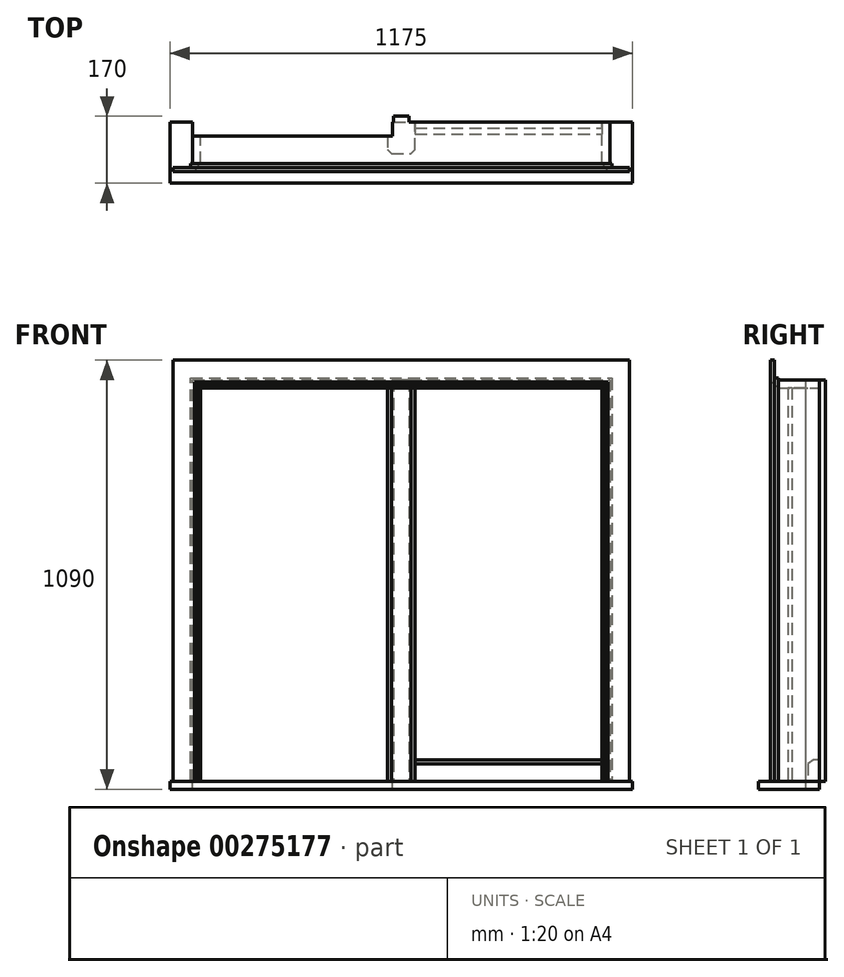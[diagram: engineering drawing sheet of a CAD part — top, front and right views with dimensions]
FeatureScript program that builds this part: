
annotation { "Feature Type Name" : "Feature", "Feature Type Description" : "" }
export const myFeature = defineFeature(function(context is Context, id is Id, definition is map)
    precondition{}
    {
        {
            var Q0;
            Q0=qCreatedBy(makeId("Top.planeOp"),FACE);
            var sketch = newSketch(context, id + "F0", { "sketchPlane" : qUnion([Q0])});
            skLineSegment(sketch, "E0.bottom", {"start": v(-530, -105) * mm, "end": v(-510, -105) * mm});
            skLineSegment(sketch, "E0.top", {"start": v(-530, 0) * mm, "end": v(-510, 0) * mm});
            skLineSegment(sketch, "E0.left", {"start": v(-530, -105) * mm, "end": v(-530, 0) * mm});
            skLineSegment(sketch, "E0.right", {"start": v(-510, -105) * mm, "end": v(-510, 0) * mm});
            skLineSegment(sketch, "E1.bottom", {"start": v(510, -105) * mm, "end": v(530, -105) * mm});
            skLineSegment(sketch, "E1.top", {"start": v(510, 0) * mm, "end": v(530, 0) * mm});
            skLineSegment(sketch, "E1.left", {"start": v(510, -105) * mm, "end": v(510, 0) * mm});
            skLineSegment(sketch, "E1.right", {"start": v(530, -105) * mm, "end": v(530, 0) * mm});
            skLineSegment(sketch, "E2", {"start": v(0, 0) * mm, "end": v(-35, 0) * mm});
            skLineSegment(sketch, "E3", {"start": v(-35, 0) * mm, "end": v(-35, -70) * mm});
            skLineSegment(sketch, "E4", {"start": v(-35, -70) * mm, "end": v(-25, -80) * mm});
            skLineSegment(sketch, "E5", {"start": v(-25, -80) * mm, "end": v(25, -80) * mm});
            skLineSegment(sketch, "E6", {"start": v(25, -80) * mm, "end": v(35, -70) * mm});
            skLineSegment(sketch, "E7", {"start": v(35, -70) * mm, "end": v(35, 0) * mm});
            skLineSegment(sketch, "E8", {"start": v(35, 0) * mm, "end": v(0, 0) * mm});
            skSolve(sketch);
        }
        {
            var Q0;
            Q0 = qSketchRegion(id + "F0", true);
            extrude(context, id + "F1", {"entities" : qUnion([Q0]), "depth" : 1000 * mm, "offsetDistance" : 25 * mm});
        }
        {
            var Q0;
            Q0=makeQuery(id+"F1.opExtrude","CAP_FACE",FACE,{"disambiguationData":[OSD([sQuery(id+"F0.wireOp",EDGE,"E0.bottom"),sQuery(id+"F0.wireOp",EDGE,"E0.top"),sQuery(id+"F0.wireOp",EDGE,"E0.left"),sQuery(id+"F0.wireOp",EDGE,"E0.right")])],"isStart":false});
            var sketch = newSketch(context, id + "F2", { "sketchPlane" : qUnion([Q0])});
            skLineSegment(sketch, "E9.bottom", {"start": v(-530, 0) * mm, "end": v(530, 0) * mm});
            skLineSegment(sketch, "E9.top", {"start": v(-530, -105) * mm, "end": v(530, -105) * mm});
            skLineSegment(sketch, "E9.left", {"start": v(-530, 0) * mm, "end": v(-530, -105) * mm});
            skLineSegment(sketch, "E9.right", {"start": v(530, 0) * mm, "end": v(530, -105) * mm});
            skSolve(sketch);
        }
        {
            var Q0;
            Q0 = qSketchRegion(id + "F2", true);
            extrude(context, id + "F3", {"entities" : qUnion([Q0]), "operationType" : NewBodyOperationType.ADD, "depth" : 20 * mm, "offsetDistance" : 25 * mm});
        }
        {
            var Q0;
            Q0=makeQuery(id+"F1.opExtrude","CAP_FACE",FACE,{"disambiguationData":[OSD([sQuery(id+"F0.wireOp",EDGE,"E2"),sQuery(id+"F0.wireOp",EDGE,"E3"),sQuery(id+"F0.wireOp",EDGE,"E4"),sQuery(id+"F0.wireOp",EDGE,"E5"),sQuery(id+"F0.wireOp",EDGE,"E6"),sQuery(id+"F0.wireOp",EDGE,"E7"),sQuery(id+"F0.wireOp",EDGE,"E8")])],"isStart":true});
            var sketch = newSketch(context, id + "F4", { "sketchPlane" : qUnion([Q0])});
            skLineSegment(sketch, "E10.bottom", {"start": v(-587.5, 0) * mm, "end": v(587.5, 0) * mm});
            skLineSegment(sketch, "E10.top", {"start": v(-587.5, 155) * mm, "end": v(587.5, 155) * mm});
            skLineSegment(sketch, "E10.left", {"start": v(-587.5, 0) * mm, "end": v(-587.5, 155) * mm});
            skLineSegment(sketch, "E10.right", {"start": v(587.5, 0) * mm, "end": v(587.5, 155) * mm});
            skSolve(sketch);
        }
        {
            var Q0;
            Q0 = qSketchRegion(id + "F4", true);
            extrude(context, id + "F5", {"entities" : qUnion([Q0]), "operationType" : NewBodyOperationType.ADD, "depth" : 20 * mm, "offsetDistance" : 25 * mm});
        }
        {
            var Q0;
            Q0=makeQuery(id+"F1.opExtrude","SWEPT_FACE",FACE,{"disambiguationData":[OSD([sQuery(id+"F0.wireOp",EDGE,"E1.left")])]});
            var sketch = newSketch(context, id + "F6", { "sketchPlane" : qUnion([Q0])});
            skLineSegment(sketch, "E11", {"start": v(0, 0) * mm, "end": v(0, 55) * mm});
            skLineSegment(sketch, "E12", {"start": v(0, 55) * mm, "end": v(15, 55) * mm});
            skLineSegment(sketch, "E13", {"start": v(15, 55) * mm, "end": v(30, 45) * mm});
            skLineSegment(sketch, "E14", {"start": v(30, 45) * mm, "end": v(30, 0) * mm});
            skLineSegment(sketch, "E15", {"start": v(30, 0) * mm, "end": v(0, 0) * mm});
            skSolve(sketch);
        }
        {
            var Q0;
            Q0=makeQuery(id+"F3.opExtrude","CAP_FACE",FACE,{"disambiguationData":[OSD([sQuery(id+"F2.wireOp",EDGE,"E9.bottom"),sQuery(id+"F2.wireOp",EDGE,"E9.top"),sQuery(id+"F2.wireOp",EDGE,"E9.left"),sQuery(id+"F2.wireOp",EDGE,"E9.right")])],"isStart":false});
            var sketch = newSketch(context, id + "F7", { "sketchPlane" : qUnion([Q0])});
            skLineSegment(sketch, "E16.bottom", {"start": v(-530, 0) * mm, "end": v(-22, 0) * mm});
            skLineSegment(sketch, "E16.top", {"start": v(-530, -35) * mm, "end": v(-22, -35) * mm});
            skLineSegment(sketch, "E16.left", {"start": v(-530, 0) * mm, "end": v(-530, -35) * mm});
            skLineSegment(sketch, "E16.right", {"start": v(-22, 0) * mm, "end": v(-22, -35) * mm});
            skSolve(sketch);
        }
        {
            var Q0;
            Q0 = qSketchRegion(id + "F7", true);
            var Q1;
            Q1=makeQuery(id+"F5.opExtrude","CAP_FACE",FACE,{"disambiguationData":[OSD([sQuery(id+"F4.wireOp",EDGE,"E10.bottom"),sQuery(id+"F4.wireOp",EDGE,"E10.top"),sQuery(id+"F4.wireOp",EDGE,"E10.left"),sQuery(id+"F4.wireOp",EDGE,"E10.right")])],"isStart":false});
            extrude(context, id + "F8", {"entities" : qUnion([Q0]), "operationType" : NewBodyOperationType.REMOVE, "endBound" : BoundingType.UP_TO_SURFACE, "oppositeDirection" : true, "depth" : 25 * mm, "endBoundEntityFace" : qUnion([Q1]), "offsetDistance" : 25 * mm});
        }
        {
            var Q0;
            Q0 = qSketchRegion(id + "F6", true);
            extrude(context, id + "F9", {"entities" : qUnion([Q0]), "operationType" : NewBodyOperationType.ADD, "endBound" : BoundingType.UP_TO_NEXT, "depth" : 25 * mm, "offsetDistance" : 25 * mm});
        }
        {
            var Q0;
            Q0=makeQuery(id+"F3.boolean.opBoolean","MERGE",FACE,{"derivedFrom":[makeQuery(id+"F1.opExtrude","SWEPT_FACE",FACE,{"disambiguationData":[OSD([sQuery(id+"F0.wireOp",EDGE,"E0.bottom")])]}),makeQuery(id+"F1.opExtrude","SWEPT_FACE",FACE,{"disambiguationData":[OSD([sQuery(id+"F0.wireOp",EDGE,"E1.bottom")])]}),makeQuery(id+"F3.opExtrude","SWEPT_FACE",FACE,{"disambiguationData":[OSD([sQuery(id+"F2.wireOp",EDGE,"E9.top")])]})]});
            var sketch = newSketch(context, id + "F10", { "sketchPlane" : qUnion([Q0])});
            skLineSegment(sketch, "E17", {"start": v(515, 0) * mm, "end": v(515, 1005) * mm});
            skLineSegment(sketch, "E18", {"start": v(515, 1005) * mm, "end": v(-515, 1005) * mm});
            skLineSegment(sketch, "E19", {"start": v(-515, 1005) * mm, "end": v(-515, 0) * mm});
            skLineSegment(sketch, "E20", {"start": v(-515, 0) * mm, "end": v(-535, 0) * mm});
            skLineSegment(sketch, "E21", {"start": v(-535, 0) * mm, "end": v(-535, 1025) * mm});
            skLineSegment(sketch, "E22", {"start": v(-535, 1025) * mm, "end": v(535, 1025) * mm});
            skLineSegment(sketch, "E23", {"start": v(535, 1025) * mm, "end": v(535, 0) * mm});
            skLineSegment(sketch, "E24", {"start": v(535, 0) * mm, "end": v(515, 0) * mm});
            skSolve(sketch);
        }
        {
            var Q0;
            Q0 = qSketchRegion(id + "F10", true);
            extrude(context, id + "F11", {"entities" : qUnion([Q0]), "operationType" : NewBodyOperationType.ADD, "depth" : 10 * mm, "offsetDistance" : 25 * mm});
        }
        {
            var Q0;
            Q0=qCreatedBy(makeId("Top.planeOp"),FACE);
            var sketch = newSketch(context, id + "F12", { "sketchPlane" : qUnion([Q0])});
            skLineSegment(sketch, "E25", {"start": v(0, 0) * mm, "end": v(20, 0) * mm});
            skLineSegment(sketch, "E26", {"start": v(20, 0) * mm, "end": v(20, 15) * mm});
            skLineSegment(sketch, "E27", {"start": v(20, 15) * mm, "end": v(-20, 15) * mm});
            skLineSegment(sketch, "E28", {"start": v(-20, 15) * mm, "end": v(-20, 0) * mm});
            skLineSegment(sketch, "E29", {"start": v(-20, 0) * mm, "end": v(0, 0) * mm});
            skSolve(sketch);
        }
        {
            var Q0;
            Q0 = qSketchRegion(id + "F12", true);
            var Q1;
            Q1=makeQuery(id+"F3.opExtrude","CAP_FACE",FACE,{"disambiguationData":[OSD([sQuery(id+"F2.wireOp",EDGE,"E9.bottom"),sQuery(id+"F2.wireOp",EDGE,"E9.top"),sQuery(id+"F2.wireOp",EDGE,"E9.left"),sQuery(id+"F2.wireOp",EDGE,"E9.right")])],"isStart":false});
            extrude(context, id + "F13", {"entities" : qUnion([Q0]), "operationType" : NewBodyOperationType.ADD, "endBound" : BoundingType.UP_TO_SURFACE, "depth" : 25 * mm, "endBoundEntityFace" : qUnion([Q1]), "offsetDistance" : 25 * mm});
        }
        {
            var Q0;
            Q0=makeQuery(id+"F11.opExtrude","CAP_FACE",FACE,{"disambiguationData":[OSD([sQuery(id+"F10.wireOp",EDGE,"E17"),sQuery(id+"F10.wireOp",EDGE,"E18"),sQuery(id+"F10.wireOp",EDGE,"E19"),sQuery(id+"F10.wireOp",EDGE,"E20"),sQuery(id+"F10.wireOp",EDGE,"E21"),sQuery(id+"F10.wireOp",EDGE,"E22"),sQuery(id+"F10.wireOp",EDGE,"E23"),sQuery(id+"F10.wireOp",EDGE,"E24")])],"isStart":false});
            var sketch = newSketch(context, id + "F14", { "sketchPlane" : qUnion([Q0])});
            skLineSegment(sketch, "E30", {"start": v(520, 0) * mm, "end": v(580, 0) * mm});
            skLineSegment(sketch, "E31", {"start": v(580, 0) * mm, "end": v(580, 1070) * mm});
            skLineSegment(sketch, "E32", {"start": v(580, 1070) * mm, "end": v(-580, 1070) * mm});
            skLineSegment(sketch, "E33", {"start": v(-580, 1070) * mm, "end": v(-580, 0) * mm});
            skLineSegment(sketch, "E34", {"start": v(-580, 0) * mm, "end": v(-520, 0) * mm});
            skLineSegment(sketch, "E35", {"start": v(-520, 0) * mm, "end": v(-520, 1010) * mm});
            skLineSegment(sketch, "E36", {"start": v(-520, 1010) * mm, "end": v(520, 1010) * mm});
            skLineSegment(sketch, "E37", {"start": v(520, 1010) * mm, "end": v(520, 0) * mm});
            skSolve(sketch);
        }
        {
            var Q0;
            Q0 = qSketchRegion(id + "F14", true);
            extrude(context, id + "F15", {"entities" : qUnion([Q0]), "operationType" : NewBodyOperationType.ADD, "depth" : 10 * mm, "offsetDistance" : 25 * mm});
        }
        {
            var Q0;
            Q0=makeQuery(id+"F15.opExtrude","CAP_EDGE",EDGE,{"disambiguationData":[OSD([sQuery(id+"F14.wireOp",EDGE,"E35")])],"isStart":false});
            var Q1;
            Q1=makeQuery(id+"F15.opExtrude","CAP_EDGE",EDGE,{"disambiguationData":[OSD([sQuery(id+"F14.wireOp",EDGE,"E36")])],"isStart":false});
            var Q2;
            Q2=makeQuery(id+"F15.opExtrude","CAP_EDGE",EDGE,{"disambiguationData":[OSD([sQuery(id+"F14.wireOp",EDGE,"E37")])],"isStart":false});
            chamfer(context, id + "F16", {"entities" : qUnion([Q0, Q1, Q2]), "chamferType" : ChamferType.TWO_OFFSETS, "width1" : 5 * mm, "oppositeDirection" : false, "width2" : 10 * mm, "tangentPropagation" : true});
        }
    });
